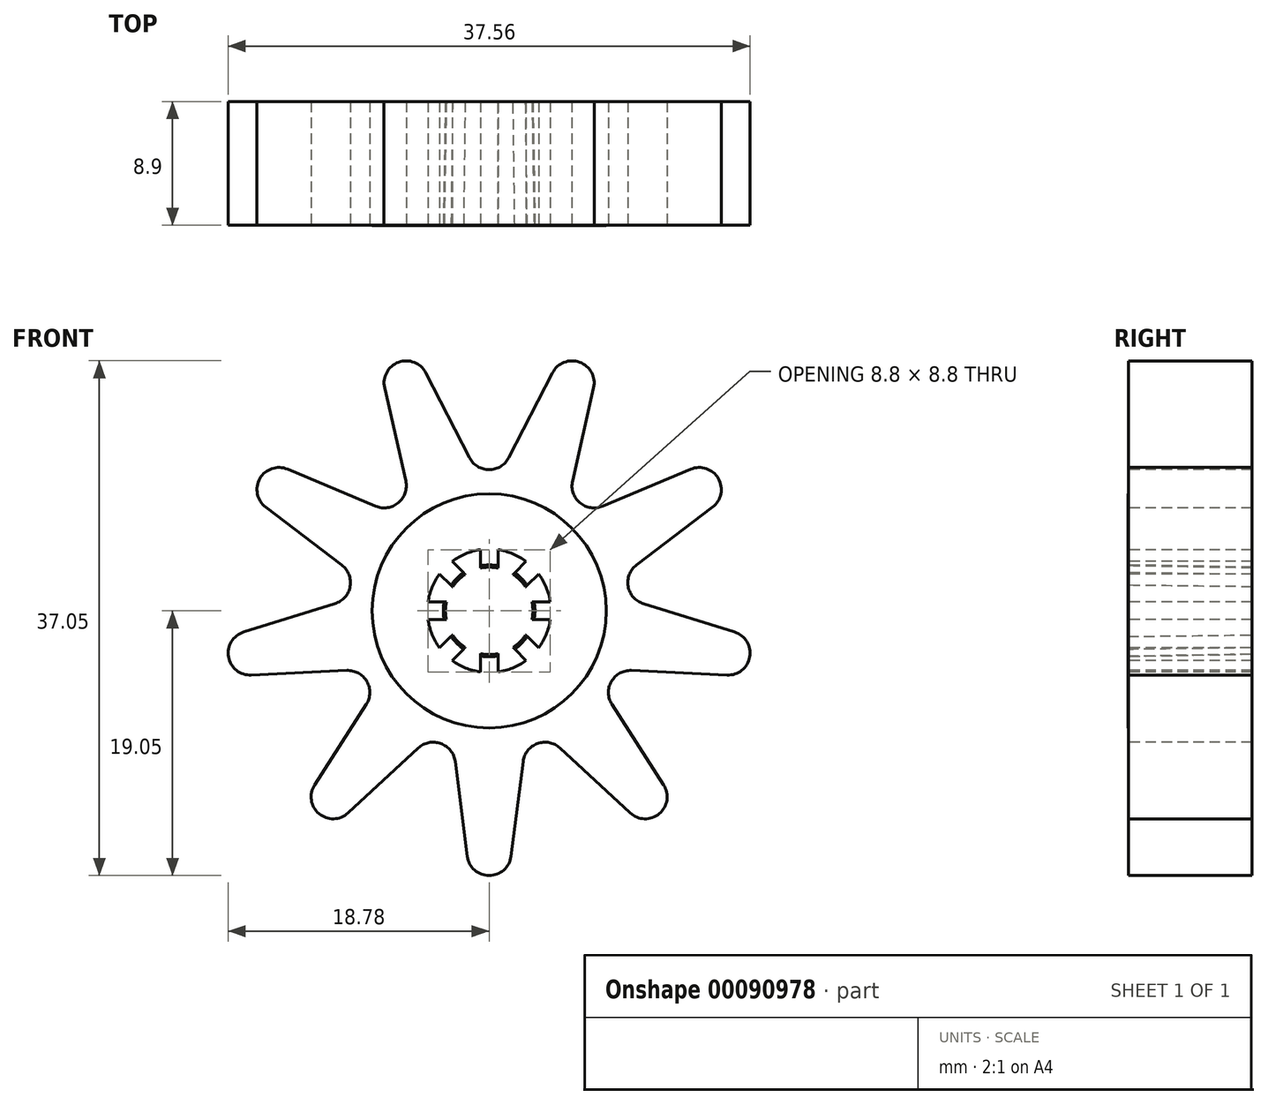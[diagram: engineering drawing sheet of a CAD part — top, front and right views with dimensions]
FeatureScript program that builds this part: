
annotation { "Feature Type Name" : "Feature", "Feature Type Description" : "" }
export const myFeature = defineFeature(function(context is Context, id is Id, definition is map)
    precondition{}
    {
        {
            var Q0;
            Q0=qCreatedBy(makeId("Front.planeOp"),FACE);
            var sketch = newSketch(context, id + "F0", { "sketchPlane" : qUnion([Q0])});
            skCircle(sketch, "E0", {"center": v(0, 0) * mm, "radius": 19.05 * mm});
            skSolve(sketch);
        }
        {
            var Q0;
            Q0=makeQuery(id+"F0.imprint","IMPRINT",FACE,{"disambiguationData":[TD([[makeQuery(id+"F0.imprint","IMPRINT",EDGE,{"derivedFrom":sQuery(id+"F0.wireOp",EDGE,"E0")}),1.0]])]});
            extrude(context, id + "F1", {"entities" : qUnion([Q0]), "oppositeDirection" : true, "depth" : 8.9 * mm});
        }
        {
            var Q0;
            Q0=makeQuery(id+"F1.opExtrude","CAP_FACE",FACE,{"disambiguationData":[OSD([sQuery(id+"F0.wireOp",EDGE,"E0")])],"isStart":true});
            var sketch = newSketch(context, id + "F2", { "sketchPlane" : qUnion([Q0])});
            skLineSegment(sketch, "E1", {"start": v(-6.93, 19.05) * mm, "end": v(0, 0) * mm, "construction": true});
            skLineSegment(sketch, "E2", {"start": v(0, 0) * mm, "end": v(6.93, 19.05) * mm, "construction": true});
            skLineSegment(sketch, "E3", {"start": v(0, 0) * mm, "end": v(0, 19.05) * mm, "construction": true});
            skLineSegment(sketch, "E4", {"start": v(-6.93, 19.05) * mm, "end": v(6.93, 19.05) * mm});
            skCircle(sketch, "E5", {"center": v(-5.97, 16.4) * mm, "radius": 1.59 * mm, "construction": true});
            skCircle(sketch, "E6", {"center": v(5.97, 16.4) * mm, "radius": 1.59 * mm, "construction": true});
            skCircle(sketch, "E7", {"center": v(0, 11.75) * mm, "radius": 1.59 * mm, "construction": true});
            skLineSegment(sketch, "E8", {"start": v(-4.56, 17.14) * mm, "end": v(-1.41, 11.02) * mm});
            skCircle(sketch, "E9", {"center": v(0, 0) * mm, "radius": 10.16 * mm, "construction": true});
            skLineSegment(sketch, "E10", {"start": v(1.41, 11.02) * mm, "end": v(4.56, 17.14) * mm});
            skArc(sketch, "E11", {"start": v(-4.56, 17.14) * mm, "mid": v(-5.4, 17.89) * mm, "end": v(-6.52, 17.9) * mm});
            skArc(sketch, "E12", {"start": v(4.56, 17.14) * mm, "mid": v(5.4, 17.89) * mm, "end": v(6.52, 17.9) * mm});
            skLineSegment(sketch, "E13", {"start": v(-6.52, 17.9) * mm, "end": v(-6.93, 19.05) * mm});
            skLineSegment(sketch, "E14", {"start": v(6.52, 17.9) * mm, "end": v(6.93, 19.05) * mm});
            skArc(sketch, "E15", {"start": v(-1.41, 11.02) * mm, "mid": v(0, 10.16) * mm, "end": v(1.41, 11.02) * mm});
            skSolve(sketch);
        }
        {
            var Q0;
            Q0 = qSketchRegion(id + "F2", true);
            var Q1;
            Q1=makeQuery(id+"F1.opExtrude","CAP_FACE",FACE,{"disambiguationData":[OSD([sQuery(id+"F0.wireOp",EDGE,"E0")])],"isStart":false});
            extrude(context, id + "F3", {"entities" : qUnion([Q0]), "endBound" : BoundingType.UP_TO_SURFACE, "oppositeDirection" : true, "endBoundEntityFace" : qUnion([Q1]), "depth" : 25.4 * mm});
        }
        {
            var Q0;
            Q0=makeQuery(id+"F3.opExtrude","SWEPT_BODY",BODY,{"disambiguationData":[OSD([sQuery(id+"F2.wireOp",EDGE,"E4"),sQuery(id+"F2.wireOp",EDGE,"E8"),sQuery(id+"F2.wireOp",EDGE,"E10"),sQuery(id+"F2.wireOp",EDGE,"E11"),sQuery(id+"F2.wireOp",EDGE,"E12"),sQuery(id+"F2.wireOp",EDGE,"E13"),sQuery(id+"F2.wireOp",EDGE,"E14"),sQuery(id+"F2.wireOp",EDGE,"E15")])]});
            var Q1;
            Q1=makeQuery(id+"F1.opExtrude","SWEPT_FACE",FACE,{"disambiguationData":[OSD([sQuery(id+"F0.wireOp",EDGE,"E0")])]});
            circularPattern(context, id + "F4", {"operationType" : NewBodyOperationType.REMOVE, "entities" : qUnion([Q0]), "axis" : qUnion([Q1]), "angle" : 360 * degree, "instanceCount" : 9, "equalSpace" : true});
        }
        {
            var Q0;
            Q0=makeQuery(id+"F1.opExtrude","CAP_FACE",FACE,{"disambiguationData":[OSD([sQuery(id+"F0.wireOp",EDGE,"E0")])],"isStart":true});
            var sketch = newSketch(context, id + "F5", { "sketchPlane" : qUnion([Q0])});
            skCircle(sketch, "E16", {"center": v(0, 0) * mm, "radius": 8.43 * mm});
            skSolve(sketch);
        }
        {
            var Q0;
            Q0 = qSketchRegion(id + "F5", true);
            extrude(context, id + "F6", {"entities" : qUnion([Q0]), "operationType" : NewBodyOperationType.ADD, "depth" : 3 / 203.2 * mm});
        }
        {
            var Q0;
            Q0=makeQuery(id+"F6.opExtrude","CAP_FACE",FACE,{"disambiguationData":[OSD([sQuery(id+"F5.wireOp",EDGE,"E16")])],"isStart":false});
            var sketch = newSketch(context, id + "F7", { "sketchPlane" : qUnion([Q0])});
            skCircle(sketch, "E17", {"center": v(0, 0) * mm, "radius": 2.67 * mm, "construction": true});
            skCircle(sketch, "E18", {"center": v(0, 0) * mm, "radius": 4.45 * mm, "construction": true});
            skLineSegment(sketch, "E19", {"start": v(0, 0) * mm, "end": v(0, 4.45) * mm, "construction": true});
            skLineSegment(sketch, "E20", {"start": v(0, 0) * mm, "end": v(4.45, 0) * mm, "construction": true});
            skLineSegment(sketch, "E21", {"start": v(0, 0) * mm, "end": v(0, -4.45) * mm, "construction": true});
            skLineSegment(sketch, "E22", {"start": v(0, 0) * mm, "end": v(-4.45, 0) * mm, "construction": true});
            skLineSegment(sketch, "E23", {"start": v(0, 0) * mm, "end": v(3.14, 3.14) * mm, "construction": true});
            skLineSegment(sketch, "E24", {"start": v(0, 0) * mm, "end": v(-3.14, 3.14) * mm, "construction": true});
            skLineSegment(sketch, "E25", {"start": v(0, 0) * mm, "end": v(3.14, -3.14) * mm, "construction": true});
            skLineSegment(sketch, "E26", {"start": v(0, 0) * mm, "end": v(-3.14, -3.14) * mm, "construction": true});
            skLineSegment(sketch, "E27", {"start": v(-0.63, 2.6) * mm, "end": v(-0.63, 4.4) * mm});
            skPoint(sketch, "E28.startSnap0", {"position": v(1.57, 1.57) * mm});
            skLineSegment(sketch, "E29", {"start": v(0.64, 2.6) * mm, "end": v(0.64, 4.4) * mm});
            skLineSegment(sketch, "E30", {"start": v(0.63, 3.5) * mm, "end": v(-0.64, 3.5) * mm, "construction": true});
            skLineSegment(sketch, "E31", {"start": v(-1.38, 2.28) * mm, "end": v(-2.66, 3.56) * mm});
            skLineSegment(sketch, "E32", {"start": v(-2.28, 1.38) * mm, "end": v(-3.56, 2.66) * mm});
            skLineSegment(sketch, "E33", {"start": v(-2.02, 2.92) * mm, "end": v(-2.92, 2.02) * mm, "construction": true});
            skLineSegment(sketch, "E34", {"start": v(-2.6, 0.64) * mm, "end": v(-4.4, 0.64) * mm});
            skLineSegment(sketch, "E35", {"start": v(-4.4, -0.64) * mm, "end": v(-2.6, -0.64) * mm});
            skLineSegment(sketch, "E36", {"start": v(-3.5, -0.64) * mm, "end": v(-3.5, 0.64) * mm, "construction": true});
            skLineSegment(sketch, "E37", {"start": v(-3.56, -2.66) * mm, "end": v(-2.28, -1.38) * mm});
            skLineSegment(sketch, "E38", {"start": v(-2.66, -3.56) * mm, "end": v(-1.38, -2.28) * mm});
            skLineSegment(sketch, "E39", {"start": v(-2.02, -2.92) * mm, "end": v(-2.92, -2.02) * mm, "construction": true});
            skLineSegment(sketch, "E40", {"start": v(-0.63, -4.4) * mm, "end": v(-0.63, -2.6) * mm});
            skLineSegment(sketch, "E41", {"start": v(0.64, -4.4) * mm, "end": v(0.64, -2.6) * mm});
            skLineSegment(sketch, "E42", {"start": v(0.64, -3.5) * mm, "end": v(-0.63, -3.5) * mm, "construction": true});
            skLineSegment(sketch, "E43", {"start": v(3.56, -2.66) * mm, "end": v(2.28, -1.38) * mm});
            skLineSegment(sketch, "E44", {"start": v(2.66, -3.56) * mm, "end": v(1.38, -2.28) * mm});
            skLineSegment(sketch, "E45", {"start": v(2.92, -2.02) * mm, "end": v(2.02, -2.92) * mm, "construction": true});
            skLineSegment(sketch, "E46", {"start": v(2.6, 0.64) * mm, "end": v(4.4, 0.64) * mm});
            skLineSegment(sketch, "E47", {"start": v(2.6, -0.64) * mm, "end": v(4.4, -0.63) * mm});
            skLineSegment(sketch, "E48", {"start": v(3.5, 0.63) * mm, "end": v(3.5, -0.64) * mm, "construction": true});
            skLineSegment(sketch, "E49", {"start": v(2.28, 1.38) * mm, "end": v(3.56, 2.66) * mm});
            skLineSegment(sketch, "E50", {"start": v(1.38, 2.28) * mm, "end": v(2.66, 3.56) * mm});
            skLineSegment(sketch, "E51", {"start": v(2.02, 2.92) * mm, "end": v(2.92, 2.02) * mm, "construction": true});
            skArc(sketch, "E52", {"start": v(0.63, 2.6) * mm, "mid": v(0, 2.67) * mm, "end": v(-0.64, 2.6) * mm});
            skArc(sketch, "E53", {"start": v(-1.38, 2.28) * mm, "mid": v(-1.89, 1.89) * mm, "end": v(-2.28, 1.38) * mm});
            skArc(sketch, "E54", {"start": v(-2.6, 0.63) * mm, "mid": v(-2.67, 0) * mm, "end": v(-2.6, -0.64) * mm});
            skArc(sketch, "E55", {"start": v(-2.28, -1.38) * mm, "mid": v(-1.89, -1.89) * mm, "end": v(-1.38, -2.28) * mm});
            skArc(sketch, "E56", {"start": v(-0.63, -2.6) * mm, "mid": v(0, -2.67) * mm, "end": v(0.64, -2.6) * mm});
            skArc(sketch, "E57", {"start": v(1.38, -2.28) * mm, "mid": v(1.89, -1.89) * mm, "end": v(2.28, -1.38) * mm});
            skArc(sketch, "E58", {"start": v(2.6, -0.64) * mm, "mid": v(2.67, 0) * mm, "end": v(2.6, 0.63) * mm});
            skArc(sketch, "E59", {"start": v(2.28, 1.38) * mm, "mid": v(1.89, 1.89) * mm, "end": v(1.38, 2.28) * mm});
            skArc(sketch, "E60", {"start": v(0.63, 4.4) * mm, "mid": v(1.7, 4.1) * mm, "end": v(2.66, 3.56) * mm});
            skArc(sketch, "E61", {"start": v(3.56, 2.66) * mm, "mid": v(4.1, 1.7) * mm, "end": v(4.4, 0.63) * mm});
            skArc(sketch, "E62", {"start": v(4.4, -0.64) * mm, "mid": v(4.1, -1.7) * mm, "end": v(3.56, -2.66) * mm});
            skArc(sketch, "E63", {"start": v(2.66, -3.56) * mm, "mid": v(1.7, -4.1) * mm, "end": v(0.64, -4.4) * mm});
            skArc(sketch, "E64", {"start": v(-0.63, -4.4) * mm, "mid": v(-1.7, -4.1) * mm, "end": v(-2.66, -3.56) * mm});
            skArc(sketch, "E65", {"start": v(-3.56, -2.66) * mm, "mid": v(-4.1, -1.7) * mm, "end": v(-4.4, -0.64) * mm});
            skArc(sketch, "E66", {"start": v(-4.4, 0.64) * mm, "mid": v(-4.1, 1.7) * mm, "end": v(-3.56, 2.66) * mm});
            skArc(sketch, "E67", {"start": v(-2.66, 3.56) * mm, "mid": v(-1.7, 4.1) * mm, "end": v(-0.63, 4.4) * mm});
            skCircle(sketch, "E68", {"center": v(0, 0) * mm, "radius": 3.18 * mm, "construction": true});
            skSolve(sketch);
        }
        {
            var Q0;
            Q0 = qSketchRegion(id + "F7", true);
            extrude(context, id + "F8", {"entities" : qUnion([Q0]), "operationType" : NewBodyOperationType.REMOVE, "oppositeDirection" : true, "depth" : 25.4 * mm});
        }
        {
            var Q0;
            Q0=makeQuery(id+"F6.opExtrude","CAP_FACE",FACE,{"disambiguationData":[OSD([sQuery(id+"F5.wireOp",EDGE,"E16")])],"isStart":false});
            var sketch = newSketch(context, id + "F9", { "sketchPlane" : qUnion([Q0])});
            skCircle(sketch, "E69", {"center": v(0, 0) * mm, "radius": 3.3 * mm});
            skSolve(sketch);
        }
        {
            var Q0;
            Q0 = qSketchRegion(id + "F9", true);
            extrude(context, id + "F10", {"entities" : qUnion([Q0]), "operationType" : NewBodyOperationType.REMOVE, "oppositeDirection" : true, "depth" : 25.4 * mm, "hasDraft" : true, "draftAngle" : 1 * degree, "draftPullDirection" : true});
        }
    });
